# Revit family: HZ 1022 en
name_source: partatom
category: Rohrzubehör
revit_build: Autodesk Revit 2017 (Build: 20160225_1515(x64)
units: mm (PartAtom-declared; Revit-internal decimal feet)

## family parameters
Arbeitsebenenbasiert = Nein
Beim Laden mit Abzugskörper schneiden = Nein
Bemaßung runder Anschluss = Durchmesser verwenden
Gemeinsam genutzt = Nein
Immer vertikal = Ja
Teiletyp = Ventil - Zerlegung in

## types (1)
- DN
    Armaturentyp = Festwiderstand (z.B. Absperrarmatur, Schmutzfänger, Druckminderer, Kondensatregler, RL-Temperaturbegrenzer, Kappenventil)
    Armaturentyp über Funktion berechnen = nein
    BIM = https://media.live.bim.site
    BIMSITE_PRODUCT_ID = ed9b19e0266cac515e9091eaba66db3f906325fc
    Beschreibung = Ausgleichswinkelabsperrung
    CONNECTOR0_DIAMETER_dY_0r = 15 mm
    CONNECTOR0_dY_00 = 114 mm
    CONNECTOR0_dY_01 = 124 mm
    CONNECTOR0_ref_dY = 114 mm
    CONNECTOR1_DIAMETER_dZ_0r = 15 mm
    CONNECTOR1_dZ_00 = 89 mm  [stored 0.291995 ft]
    CONNECTOR1_dZ_01 = 99 mm
    CONNECTOR1_ref_dZ = 89 mm  [stored 0.291995 ft]
    DATANORM = 1022
    GTIN = 4022023301113
    HAN = 1022
    HeinzeBIM = https://www.heinze.de
    Hersteller = Hans Weitzel
    Ist System = Nein
    Ist Zubehör = Nein
    Masse (netto) [kg] = 0.35
    Maximaler Betriebsdruck (Arbeitsdruck) ps [bar] = 0.0001
    Nenndruck = 10
    Nenndrucksystem = PN
    Nennmaß = 15
    Nennweite DN = 15
    Nennweitensystem = DN
    Produktbeschreibung = HZ-Ausgleichswinkelabsperrung AWA mit HZ-Klemmringverschr. Nr 1034 für HKU
    Produktbezeichnung = Heizkörperarmaturen für Zweirohrsysteme
    Produktklassifikation = AWA Ausgleichswinkelabsperrung
    Regelcharakteristik der Armatur = 1
    Typname = HZ-Ausgleichswinkelabsperrung AWA mit HZ-Klemmringverschr. Nr 1034 für HKU
    URL = https://www.hz-weitzel.de
    VDIBSN = 0020030000020000001000000000150010000000000000000100000000
    Variante/Varianten-Art/Zubehörbezeichnung = Durchgang
    Warenhauptgruppe = Heizkörper- u. Heizungsarmaturen
    voreinstellbar/Einsatz a) = 0

note: [stored X ft] marks values corroborated as IEEE doubles in the binary element streams (Revit-internal decimal feet)
